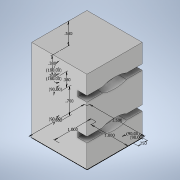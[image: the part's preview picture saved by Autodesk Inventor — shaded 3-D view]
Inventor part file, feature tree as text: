
AUTODESK INVENTOR PART (.ipt)
format: ipt  version: 2020 (Build 240168000, 168)  size: 166,400 bytes
history: native  units: in
note: dims shown in document units (in); Inventor stores cm internally (conversion verified against a paired STEP export)
features: extrude x4, sketch x3, hole x1
ambient origin geometry x8: Origin, YZ Plane, XZ Plane, XY Plane, X Axis, Y Axis, Z Axis, Center Point
bodies: Solid1 (feature_tree)
feature tree (8):
  sketch  "Sketch1"  dims[d0=1.5in d1=1.5in]
  extrude  "Extrusion1"  Depth=1.5in
  hole  "Hole1"  [1 undecoded]
  sketch  "Sketch2"  dims[d2=0.25in d3=90.0deg]
  extrude  "Extrusion2"  TaperAngle=90.0deg  [1 undecoded]
  extrude  "Extrusion3"  Depth=0.25in
  extrude  "Extrusion4"  Depth=2.24in TaperAngle=0.0deg
  sketch  "Sketch3"  dims[d4=1.0in d5=90.0deg d6=1.0in d7=2.24in d8=0.0in d9=0.3125in d10=0.75in d11=0.438in d12=0.25in d13=0.5635in d14=0.5in d15=0.0in d16=0.7in d17=90.0deg d18=0.38in d19=90.0deg d20=0.2in d21=180.0deg d22=0.38in d23=180.0deg d24=1.25in d25=0.0in d26=1.5in d27=0.0in d28=0.15in d29=0.15in d30=0.25in d31=0.0in d32=0.58in]
note: 2 required parameter values undecoded (feature->parameter linkage not recoverable at this tier; creation-order binding heuristic only, values carry confidence <= 0.55)
